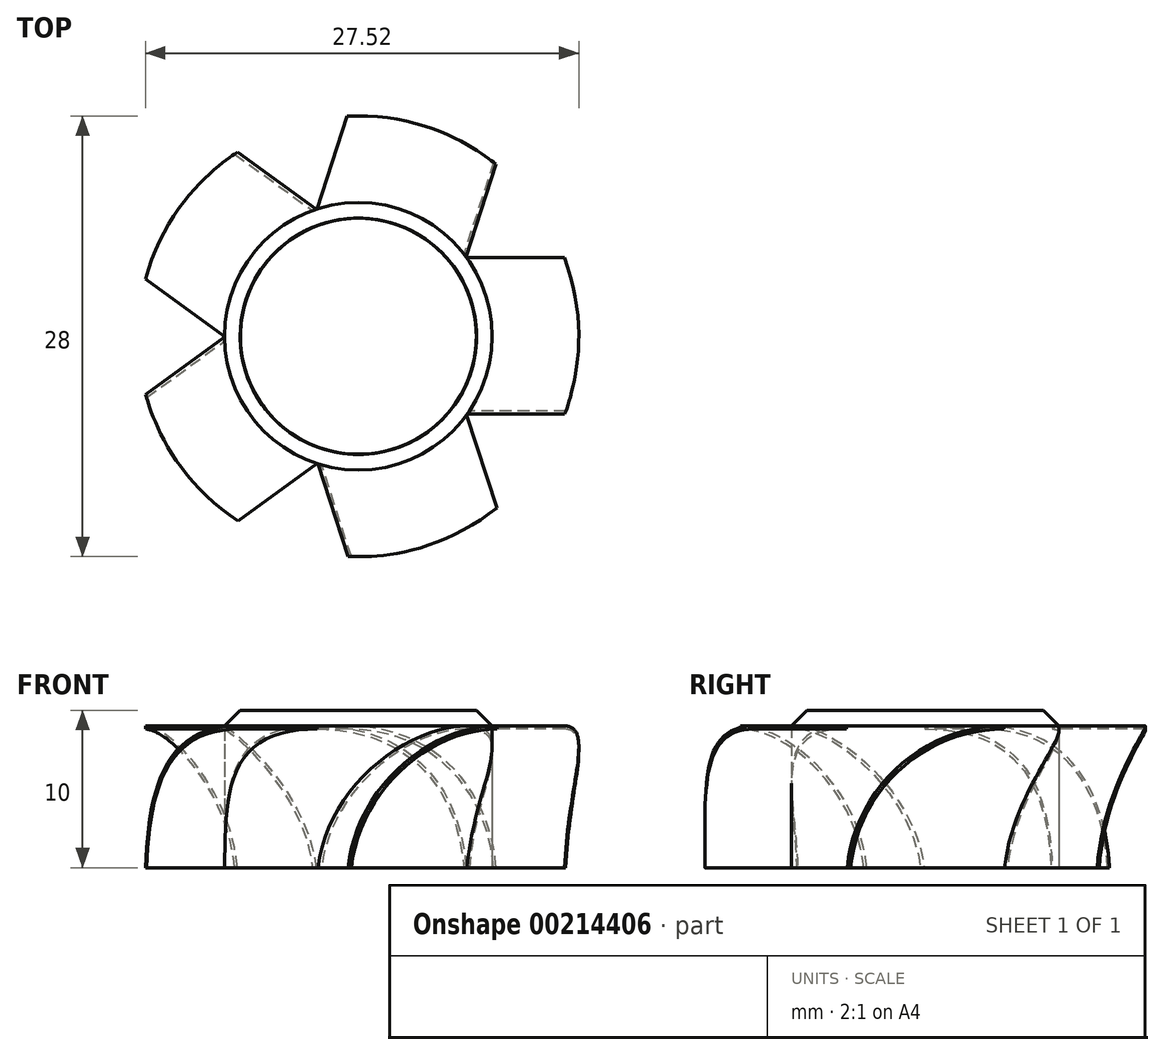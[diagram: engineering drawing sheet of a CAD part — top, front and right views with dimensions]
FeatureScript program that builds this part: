
annotation { "Feature Type Name" : "Feature", "Feature Type Description" : "" }
export const myFeature = defineFeature(function(context is Context, id is Id, definition is map)
    precondition{}
    {
        {
            var Q0;
            Q0=qCreatedBy(makeId("Top.planeOp"),FACE);
            var sketch = newSketch(context, id + "F0", { "sketchPlane" : qUnion([Q0])});
            skCircle(sketch, "E0", {"center": v(0, 0) * mm, "radius": 8.5 * mm});
            skSolve(sketch);
        }
        {
            var Q0;
            Q0 = qSketchRegion(id + "F0", true);
            extrude(context, id + "F1", {"entities" : qUnion([Q0]), "depth" : 10 * mm});
        }
        {
            var Q0;
            Q0=makeQuery(id+"F1.opExtrude","CAP_EDGE",EDGE,{"disambiguationData":[OSD([sQuery(id+"F0.wireOp",EDGE,"E0")])],"isStart":false});
            chamfer(context, id + "F2", {"entities" : qUnion([Q0]), "width" : 1 * mm, "tangentPropagation" : true});
        }
        {
            var Q0;
            Q0=qCreatedBy(makeId("Right.planeOp"),FACE);
            var sketch = newSketch(context, id + "F3", { "sketchPlane" : qUnion([Q0])});
            skArc(sketch, "E1", {"start": v(5, 9) * mm, "mid": v(-1.7, 6.42) * mm, "end": v(-4.95, 0) * mm});
            skLineSegment(sketch, "E2", {"start": v(0, 9) * mm, "end": v(5, 9) * mm, "construction": true});
            skArc(sketch, "E3.0", {"start": v(5, 8.8) * mm, "mid": v(-1.57, 6.27) * mm, "end": v(-4.75, 0) * mm});
            skLineSegment(sketch, "E4", {"start": v(5, 8.8) * mm, "end": v(5, 9) * mm});
            skLineSegment(sketch, "E5", {"start": v(-4.95, 0) * mm, "end": v(-4.75, 0) * mm});
            skSolve(sketch);
        }
        {
            var Q0;
            Q0 = qSketchRegion(id + "F3", true);
            extrude(context, id + "F4", {"entities" : qUnion([Q0]), "operationType" : NewBodyOperationType.ADD, "depth" : 25 * mm});
        }
        {
            var Q0;
            Q0=qCreatedBy(makeId("Right.planeOp"),FACE);
            var sketch = newSketch(context, id + "F5", { "sketchPlane" : qUnion([Q0])});
            skLineSegment(sketch, "E6", {"start": v(0, 0) * mm, "end": v(0, 16.86) * mm, "construction": true});
            skSolve(sketch);
        }
        {
            var Q0;
            Q0=makeQuery(id+"F1.opExtrude","SWEPT_BODY",BODY,{"disambiguationData":[OSD([sQuery(id+"F0.wireOp",EDGE,"E0")])]});
            var Q1;
            Q1=sQuery(id+"F5.wireOp",EDGE,"E6");
            circularPattern(context, id + "F6", {"entities" : qUnion([Q0]), "axis" : qUnion([Q1]), "angle" : 360 * degree, "instanceCount" : 5, "equalSpace" : true});
        }
        {
            var Q0;
            Q0=qCreatedBy(makeId("Top.planeOp"),FACE);
            var sketch = newSketch(context, id + "F7", { "sketchPlane" : qUnion([Q0])});
            skCircle(sketch, "E7", {"center": v(0, 0) * mm, "radius": 14 * mm});
            skCircle(sketch, "E8", {"center": v(0, 0) * mm, "radius": 30 * mm});
            skSolve(sketch);
        }
        {
            var Q0;
            Q0 = qSketchRegion(id + "F7", true);
            extrude(context, id + "F8", {"entities" : qUnion([Q0]), "operationType" : NewBodyOperationType.REMOVE, "depth" : 25 * mm});
        }
    });
